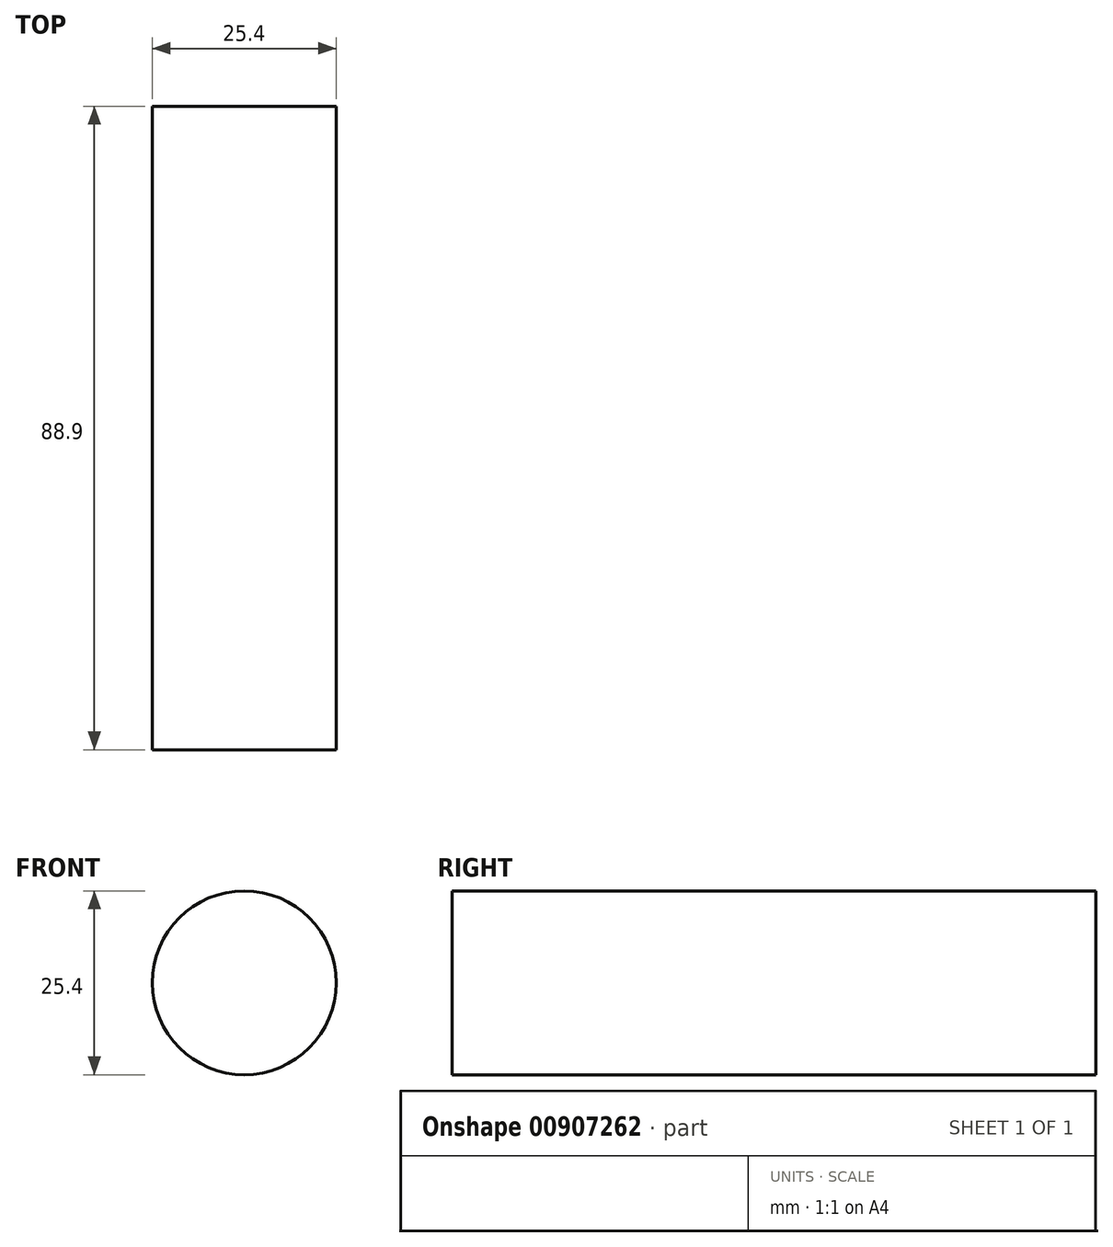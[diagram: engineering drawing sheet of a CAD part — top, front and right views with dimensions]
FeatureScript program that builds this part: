
annotation { "Feature Type Name" : "Feature", "Feature Type Description" : "" }
export const myFeature = defineFeature(function(context is Context, id is Id, definition is map)
    precondition{}
    {
        {
            var Q0;
            Q0=qCreatedBy(makeId("Front.planeOp"),FACE);
            var sketch = newSketch(context, id + "F0", { "sketchPlane" : qUnion([Q0])});
            skCircle(sketch, "E0", {"center": v(0, 0) * mm, "radius": 12.7 * mm});
            skSolve(sketch);
        }
        {
            var Q0;
            Q0 = qSketchRegion(id + "F0", true);
            extrude(context, id + "F1", {"entities" : qUnion([Q0]), "depth" : 88.9 * mm, "offsetDistance" : 25.4 * mm});
        }
    });
